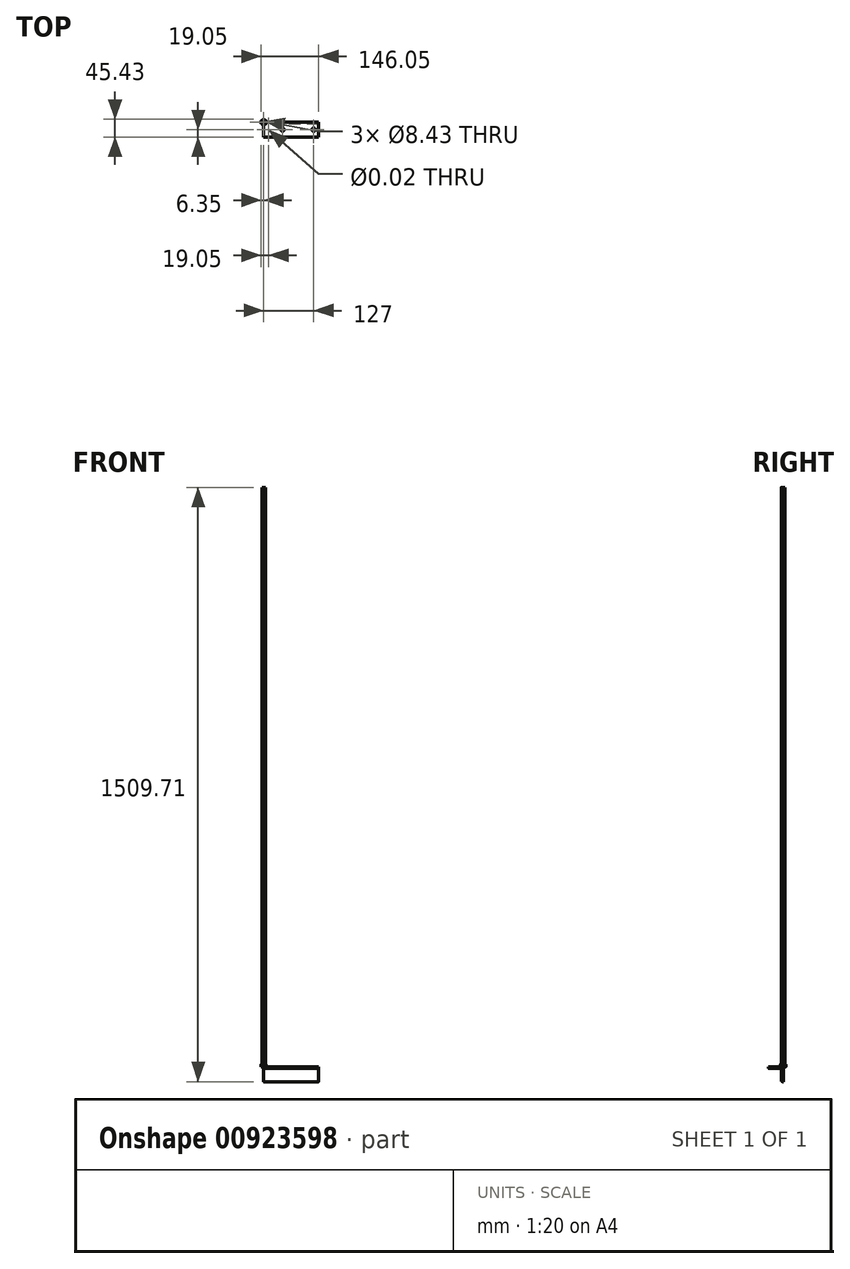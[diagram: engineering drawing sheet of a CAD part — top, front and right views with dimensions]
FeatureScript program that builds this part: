
annotation { "Feature Type Name" : "Feature", "Feature Type Description" : "" }
export const myFeature = defineFeature(function(context is Context, id is Id, definition is map)
    precondition{}
    {
        {
            var Q0;
            Q0=qCreatedBy(makeId("Right.planeOp"),FACE);
            var sketch = newSketch(context, id + "F0", { "sketchPlane" : qUnion([Q0])});
            skLineSegment(sketch, "E0", {"start": v(0, 0) * mm, "end": v(0, -38.1) * mm});
            skLineSegment(sketch, "E1", {"start": v(0, 0) * mm, "end": v(-38.1, 0) * mm});
            skLineSegment(sketch, "E2.0", {"start": v(-7.94, -4.76) * mm, "end": v(-34.93, -4.76) * mm});
            skLineSegment(sketch, "E2.1", {"start": v(-4.76, -7.94) * mm, "end": v(-4.76, -34.93) * mm});
            skLineSegment(sketch, "E3", {"start": v(-38.1, 0) * mm, "end": v(-38.1, -1.59) * mm});
            skLineSegment(sketch, "E4", {"start": v(0, -38.1) * mm, "end": v(-1.59, -38.1) * mm});
            skPoint(sketch, "E5.visualSharp", {"position": v(-38.1, -4.76) * mm});
            skArc(sketch, "E5.filletArc", {"start": v(-38.1, -1.59) * mm, "mid": v(-37.17, -3.83) * mm, "end": v(-34.93, -4.76) * mm});
            skPoint(sketch, "E6.visualSharp", {"position": v(-4.76, -4.76) * mm});
            skArc(sketch, "E6.filletArc", {"start": v(-4.76, -7.94) * mm, "mid": v(-5.7, -5.7) * mm, "end": v(-7.94, -4.76) * mm});
            skPoint(sketch, "E7.visualSharp", {"position": v(-4.76, -38.1) * mm});
            skArc(sketch, "E7.filletArc", {"start": v(-4.76, -34.93) * mm, "mid": v(-3.83, -37.17) * mm, "end": v(-1.59, -38.1) * mm});
            skSolve(sketch);
        }
        {
            var Q0;
            Q0 = qSketchRegion(id + "F0", true);
            extrude(context, id + "F1", {"entities" : qUnion([Q0]), "depth" : 139.7 * mm, "offsetDistance" : 25.4 * mm});
        }
        {
            var Q0;
            Q0=makeQuery(id+"F1.opExtrude","SWEPT_FACE",FACE,{"disambiguationData":[OSD([sQuery(id+"F0.wireOp",EDGE,"E1")])]});
            var sketch = newSketch(context, id + "F2", { "sketchPlane" : qUnion([Q0])});
            skLineSegment(sketch, "E8", {"start": v(0, -19.05) * mm, "end": v(139.7, -19.05) * mm, "construction": true});
            skLineSegment(sketch, "E9", {"start": v(12.7, 0) * mm, "end": v(12.7, -38.1) * mm, "construction": true});
            skLineSegment(sketch, "E10", {"start": v(47.63, 0) * mm, "end": v(47.63, -38.1) * mm, "construction": true});
            skLineSegment(sketch, "E11", {"start": v(127, 0) * mm, "end": v(127, -38.1) * mm, "construction": true});
            skPoint(sketch, "E12", {"position": v(12.7, -19.05) * mm});
            skPoint(sketch, "E13", {"position": v(47.63, -19.05) * mm});
            skPoint(sketch, "E14", {"position": v(127, -19.05) * mm});
            skSolve(sketch);
        }
        {
            var Q0;
            Q0=sQuery(id+"F2.wireOp",VERTEX,"E13");
            var Q1;
            Q1=sQuery(id+"F2.wireOp",VERTEX,"E14");
            var Q2;
            Q2=makeQuery(id+"F1.opExtrude","SWEPT_BODY",BODY,{"disambiguationData":[OSD([sQuery(id+"F0.wireOp",EDGE,"E0"),sQuery(id+"F0.wireOp",EDGE,"E1"),sQuery(id+"F0.wireOp",EDGE,"E2.0"),sQuery(id+"F0.wireOp",EDGE,"E2.1"),sQuery(id+"F0.wireOp",EDGE,"E3"),sQuery(id+"F0.wireOp",EDGE,"E4"),sQuery(id+"F0.wireOp",EDGE,"E5.filletArc"),sQuery(id+"F0.wireOp",EDGE,"E6.filletArc"),sQuery(id+"F0.wireOp",EDGE,"E7.filletArc")])]});
            hole(context, id + "F3", {"style" : HoleStyle.SIMPLE, "endStyle" : HoleEndStyle.THROUGH, "standardTappedOrClearance" : lookupTablePath({ "standard" : "ANSI", "fit" : "Normal (ASME)", "engagement" : "75%", "pitch" : "24 tpi", "size" : "3/8", "type" : "Tapped" }), "standardBlindInLast" : lookupTablePath({ "fit" : "Normal", "standard" : "ANSI", "engagement" : "75%", "pitch" : "24 tpi", "size" : "3/8", "type" : "Tapped" }), "holeDiameter" : 8.43 * mm, "majorDiameter" : 9.52 * mm, "showTappedDepth" : true, "isTappedThrough" : true, "tappedDepth" : 12.7 * mm, "tapClearance" : 3, "locations" : qUnion([Q0, Q1]), "scope" : qUnion([Q2])});
        }
        {
            var Q0;
            Q0=sQuery(id+"F2.wireOp",VERTEX,"E12");
            var Q1;
            Q1=makeQuery(id+"F1.opExtrude","SWEPT_BODY",BODY,{"disambiguationData":[OSD([sQuery(id+"F0.wireOp",EDGE,"E0"),sQuery(id+"F0.wireOp",EDGE,"E1"),sQuery(id+"F0.wireOp",EDGE,"E2.0"),sQuery(id+"F0.wireOp",EDGE,"E2.1"),sQuery(id+"F0.wireOp",EDGE,"E3"),sQuery(id+"F0.wireOp",EDGE,"E4"),sQuery(id+"F0.wireOp",EDGE,"E5.filletArc"),sQuery(id+"F0.wireOp",EDGE,"E6.filletArc"),sQuery(id+"F0.wireOp",EDGE,"E7.filletArc")])]});
            hole(context, id + "F4", {"style" : HoleStyle.SIMPLE, "endStyle" : HoleEndStyle.THROUGH, "standardTappedOrClearance" : lookupTablePath({ "standard" : "ANSI", "fit" : "Normal (ASME)", "size" : "1/2 (0.5)", "type" : "Drilled" }), "standardBlindInLast" : lookupTablePath({ "fit" : "Normal", "standard" : "ANSI", "size" : "1/2", "type" : "Drilled" }), "holeDiameter" : 1 / 50.8 * mm, "majorDiameter" : 6.35 * mm, "isTappedThrough" : true, "tappedDepth" : 12.7 * mm, "tapClearance" : 3, "locations" : qUnion([Q0]), "scope" : qUnion([Q1])});
        }
        {
            var Q0;
            Q0=qCreatedBy(makeId("Top.planeOp"),FACE);
            var sketch = newSketch(context, id + "F5", { "sketchPlane" : qUnion([Q0])});
            skCircle(sketch, "E15", {"center": v(0, 0) * mm, "radius": 4.76 * mm});
            skSolve(sketch);
        }
        {
            var Q0;
            Q0 = qSketchRegion(id + "F5", true);
            extrude(context, id + "F6", {"entities" : qUnion([Q0]), "depth" : 169.86 * mm, "offsetDistance" : 25.4 * mm});
        }
        {
            var Q0;
            Q0 = qSketchRegion(id + "F5", true);
            extrude(context, id + "F7", {"entities" : qUnion([Q0]), "depth" : 1471.6 * mm, "offsetDistance" : 25.4 * mm});
        }
        {
            var Q0;
            Q0 = qSketchRegion(id + "F5", true);
            extrude(context, id + "F8", {"entities" : qUnion([Q0]), "depth" : 473.07 * mm, "offsetDistance" : 25.4 * mm});
        }
        {
            var Q0;
            Q0=qCreatedBy(makeId("Top.planeOp"),FACE);
            var sketch = newSketch(context, id + "F9", { "sketchPlane" : qUnion([Q0])});
            skCircle(sketch, "E16.cCircle", {"center": v(0, 0) * mm, "radius": 6.35 * mm, "construction": true});
            skLineSegment(sketch, "E16.0", {"start": v(6.35, 3.67) * mm, "end": v(6.35, -3.67) * mm});
            skLineSegment(sketch, "E16.1", {"start": v(6.35, -3.67) * mm, "end": v(0, -7.33) * mm});
            skLineSegment(sketch, "E16.2", {"start": v(0, -7.33) * mm, "end": v(-6.35, -3.67) * mm});
            skLineSegment(sketch, "E16.3", {"start": v(-6.35, -3.67) * mm, "end": v(-6.35, 3.67) * mm});
            skLineSegment(sketch, "E16.4", {"start": v(-6.35, 3.67) * mm, "end": v(0, 7.33) * mm});
            skLineSegment(sketch, "E16.5", {"start": v(0, 7.33) * mm, "end": v(6.35, 3.67) * mm});
            skPoint(sketch, "E16.0.midPoint", {"position": v(6.35, 0) * mm});
            skCircle(sketch, "E17", {"center": v(0, 0) * mm, "radius": 4.22 * mm});
            skSolve(sketch);
        }
        {
            var Q0;
            Q0=makeQuery(id+"F9.imprint","IMPRINT",FACE,{"disambiguationData":[TD([[makeQuery(id+"F9.imprint","IMPRINT",EDGE,{"derivedFrom":sQuery(id+"F9.wireOp",EDGE,"E16.0")}),-1.0]])]});
            extrude(context, id + "F10", {"entities" : qUnion([Q0]), "depth" : 6.35 * mm, "offsetDistance" : 25.4 * mm});
        }
        {
            var Q0;
            Q0=qCreatedBy(makeId("Right.planeOp"),FACE);
            var sketch = newSketch(context, id + "F11", { "sketchPlane" : qUnion([Q0])});
            skLineSegment(sketch, "E18", {"start": v(6.35, 6.35) * mm, "end": v(7.94, 6.35) * mm});
            skLineSegment(sketch, "E19", {"start": v(7.94, 6.35) * mm, "end": v(7.94, 5.92) * mm});
            skLineSegment(sketch, "E20", {"start": v(7.94, 5.92) * mm, "end": v(6.35, 6.35) * mm});
            skLineSegment(sketch, "E21", {"start": v(6.35, 0) * mm, "end": v(7.94, 0) * mm});
            skLineSegment(sketch, "E22", {"start": v(7.94, 0) * mm, "end": v(7.94, 0.43) * mm});
            skLineSegment(sketch, "E23", {"start": v(7.94, 0.43) * mm, "end": v(6.35, 0) * mm});
            skLineSegment(sketch, "E24", {"start": v(0, -2.05) * mm, "end": v(0, 7.9) * mm, "construction": true});
            skSolve(sketch);
        }
        {
            var Q0;
            Q0 = qSketchRegion(id + "F11", true);
            var Q1;
            Q1=sQuery(id+"F11.wireOp",EDGE,"E24");
            revolve(context, id + "F12", {"operationType" : NewBodyOperationType.REMOVE, "surfaceOperationType" : NewSurfaceOperationType.NEW, "entities" : qUnion([Q0]), "axis" : qUnion([Q1]), "revolveType" : RevolveType.FULL, "oppositeDirection" : true});
        }
        {
            var Q0;
            Q0=makeQuery(id+"F10.opExtrude","CAP_EDGE",EDGE,{"disambiguationData":[OSD([sQuery(id+"F9.wireOp",EDGE,"E17")])],"isStart":false});
            var Q1;
            Q1=makeQuery(id+"F10.opExtrude","CAP_EDGE",EDGE,{"disambiguationData":[OSD([sQuery(id+"F9.wireOp",EDGE,"E17")])],"isStart":true});
            chamfer(context, id + "F13", {"entities" : qUnion([Q0, Q1]), "chamferType" : ChamferType.OFFSET_ANGLE, "width" : 0.4 * mm, "oppositeDirection" : false, "angle" : 45 * degree, "tangentPropagation" : true});
        }
    });
